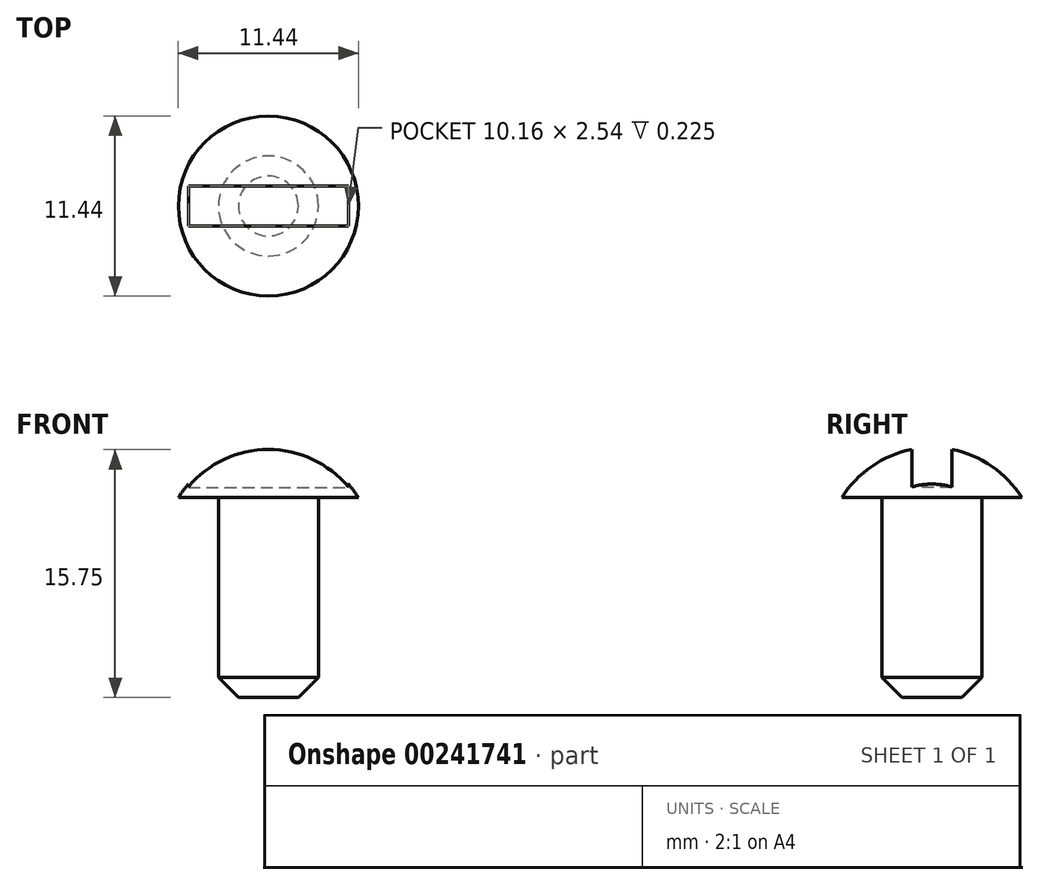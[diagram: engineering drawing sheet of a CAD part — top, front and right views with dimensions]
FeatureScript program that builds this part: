
annotation { "Feature Type Name" : "Feature", "Feature Type Description" : "" }
export const myFeature = defineFeature(function(context is Context, id is Id, definition is map)
    precondition{}
    {
        {
            var Q0;
            Q0=qCreatedBy(makeId("Front.planeOp"),FACE);
            var sketch = newSketch(context, id + "F0", { "sketchPlane" : qUnion([Q0])});
            skLineSegment(sketch, "E0", {"start": v(0, 0) * mm, "end": v(0, 0) * mm});
            skLineSegment(sketch, "E1", {"start": v(0, 0) * mm, "end": v(3.17, 0) * mm});
            skLineSegment(sketch, "E2", {"start": v(3.17, 0) * mm, "end": v(3.17, 12.7) * mm});
            skLineSegment(sketch, "E3", {"start": v(3.17, 12.7) * mm, "end": v(5.72, 12.7) * mm});
            skLineSegment(sketch, "E4", {"start": v(0, 15.88) * mm, "end": v(0, 0) * mm});
            skArc(sketch, "E5", {"start": v(0, 15.88) * mm, "mid": v(3.27, 15.03) * mm, "end": v(5.72, 12.7) * mm});
            skSolve(sketch);
        }
        {
            var Q0;
            Q0=makeQuery(id+"F0.imprint","IMPRINT",FACE,{"disambiguationData":[TD([[makeQuery(id+"F0.imprint","IMPRINT",EDGE,{"derivedFrom":sQuery(id+"F0.wireOp",EDGE,"E1")}),1.0]])]});
            var Q1;
            Q1=sQuery(id+"F0.wireOp",EDGE,"E4");
            revolve(context, id + "F1", {"entities" : qUnion([Q0]), "axis" : qUnion([Q1]), "revolveType" : RevolveType.FULL});
        }
        {
            var Q0;
            Q0=makeQuery(id+"F1.opRevolve","SWEPT_FACE",FACE,{"disambiguationData":[OSD([sQuery(id+"F0.wireOp",EDGE,"E3")])]});
            cPlane(context, id + "F2", {"entities" : qUnion([Q0]), "cplaneType" : CPlaneType.OFFSET, "offset" : 0.64 * mm, "oppositeDirection" : true, "width" : 152.4 * mm, "height" : 152.4 * mm});
        }
        {
            var Q0;
            Q0=qCreatedBy(id+"F2.planeOp",FACE);
            var sketch = newSketch(context, id + "F3", { "sketchPlane" : qUnion([Q0])});
            skLineSegment(sketch, "E6.bottom", {"start": v(-5.08, -1.27) * mm, "end": v(5.08, -1.27) * mm});
            skLineSegment(sketch, "E6.top", {"start": v(-5.08, 1.27) * mm, "end": v(5.08, 1.27) * mm});
            skLineSegment(sketch, "E6.left", {"start": v(-5.08, -1.27) * mm, "end": v(-5.08, 1.27) * mm});
            skLineSegment(sketch, "E6.right", {"start": v(5.08, -1.27) * mm, "end": v(5.08, 1.27) * mm});
            skPoint(sketch, "E6.middle", {"position": v(0, 0) * mm});
            skSolve(sketch);
        }
        {
            var Q0;
            Q0 = qSketchRegion(id + "F3", true);
            extrude(context, id + "F4", {"entities" : qUnion([Q0]), "operationType" : NewBodyOperationType.REMOVE, "oppositeDirection" : true, "depth" : 6.15 * mm});
        }
        {
            var Q0;
            Q0=makeQuery(id+"F1.opRevolve","SWEPT_FACE",FACE,{"disambiguationData":[OSD([sQuery(id+"F0.wireOp",EDGE,"E1")])]});
            chamfer(context, id + "F5", {"entities" : qUnion([Q0]), "width" : 1.27 * mm, "tangentPropagation" : true});
        }
    });
